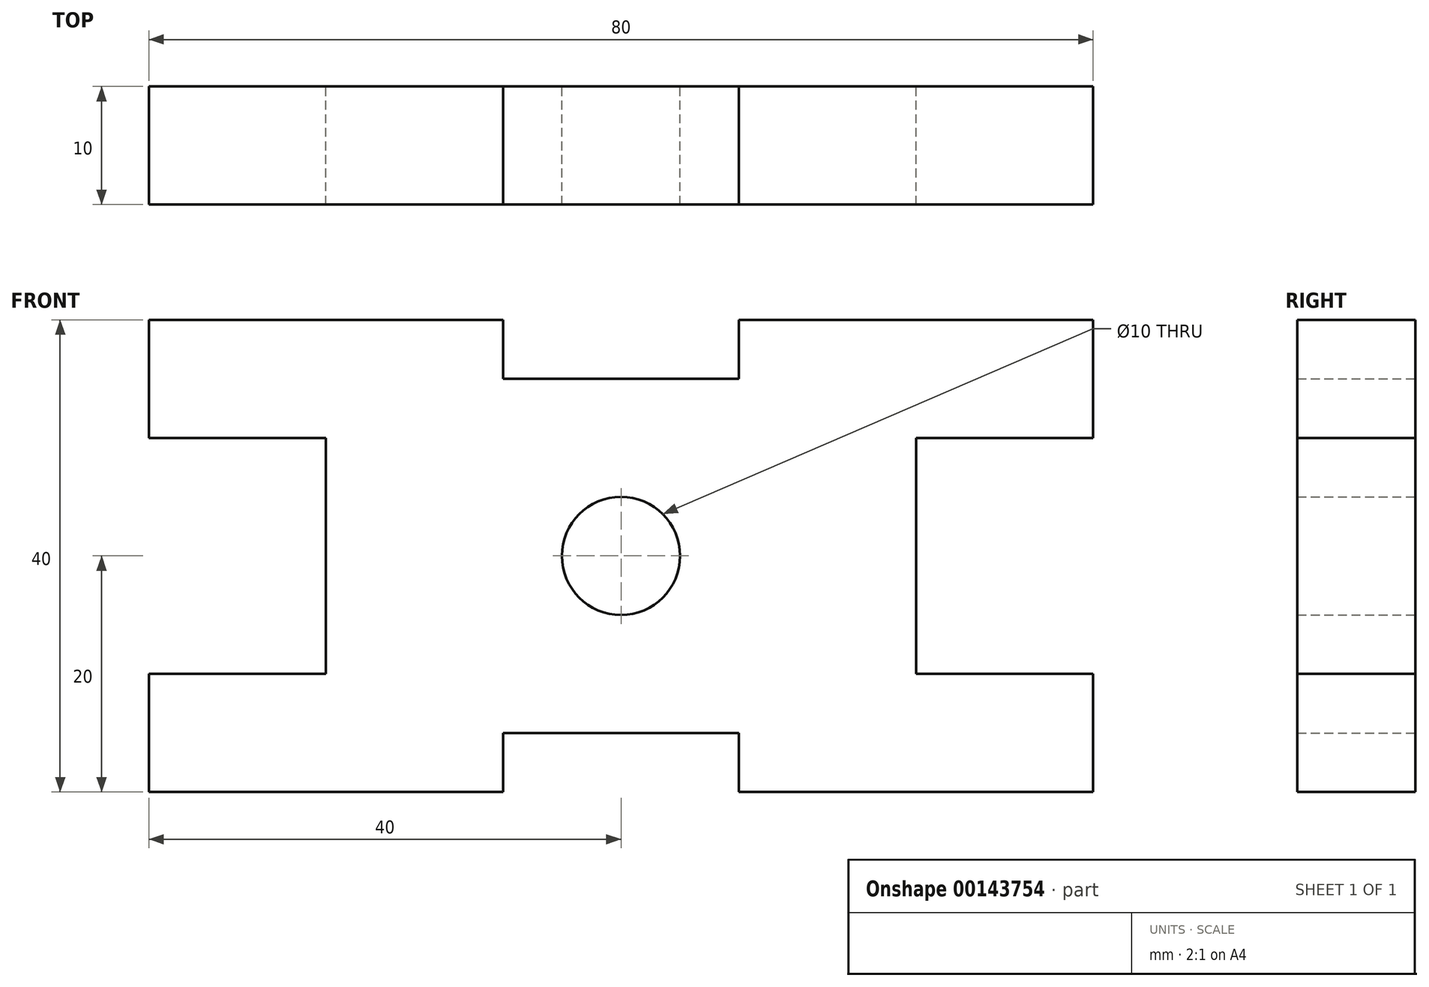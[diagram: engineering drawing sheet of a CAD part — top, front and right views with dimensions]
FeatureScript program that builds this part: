
annotation { "Feature Type Name" : "Feature", "Feature Type Description" : "" }
export const myFeature = defineFeature(function(context is Context, id is Id, definition is map)
    precondition{}
    {
        {
            var Q0;
            Q0=qCreatedBy(makeId("Front.planeOp"),FACE);
            var sketch = newSketch(context, id + "F0", { "sketchPlane" : qUnion([Q0])});
            skLineSegment(sketch, "E0", {"start": v(25, 10) * mm, "end": v(25, -10) * mm});
            skLineSegment(sketch, "E1", {"start": v(25, 10) * mm, "end": v(40, 10) * mm});
            skLineSegment(sketch, "E2", {"start": v(40, 10) * mm, "end": v(40, 20) * mm});
            skLineSegment(sketch, "E3", {"start": v(25, -10) * mm, "end": v(40, -10) * mm});
            skLineSegment(sketch, "E4", {"start": v(40, -10) * mm, "end": v(40, -20) * mm});
            skLineSegment(sketch, "E5", {"start": v(40, 20) * mm, "end": v(10, 20) * mm});
            skLineSegment(sketch, "E6", {"start": v(10, 20) * mm, "end": v(10, 15) * mm});
            skLineSegment(sketch, "E7", {"start": v(10, 15) * mm, "end": v(-10, 15) * mm});
            skLineSegment(sketch, "E8", {"start": v(-10, 15) * mm, "end": v(-10, 20) * mm});
            skLineSegment(sketch, "E9", {"start": v(-10, 20) * mm, "end": v(-40, 20) * mm});
            skLineSegment(sketch, "E10", {"start": v(-40, 20) * mm, "end": v(-40, 10) * mm});
            skLineSegment(sketch, "E11", {"start": v(-40, 10) * mm, "end": v(-25, 10) * mm});
            skLineSegment(sketch, "E12", {"start": v(-25, 10) * mm, "end": v(-25, -10) * mm});
            skLineSegment(sketch, "E13", {"start": v(-25, -10) * mm, "end": v(-40, -10) * mm});
            skLineSegment(sketch, "E14", {"start": v(-40, -10) * mm, "end": v(-40, -20) * mm});
            skLineSegment(sketch, "E15", {"start": v(-40, -20) * mm, "end": v(-10, -20) * mm});
            skLineSegment(sketch, "E16", {"start": v(-10, -20) * mm, "end": v(-10, -15) * mm});
            skLineSegment(sketch, "E17", {"start": v(-10, -15) * mm, "end": v(10, -15) * mm});
            skLineSegment(sketch, "E18", {"start": v(10, -15) * mm, "end": v(10, -20) * mm});
            skLineSegment(sketch, "E19", {"start": v(10, -20) * mm, "end": v(40, -20) * mm});
            skLineSegment(sketch, "E20", {"start": v(0, 15) * mm, "end": v(0, -15) * mm, "construction": true});
            skLineSegment(sketch, "E21", {"start": v(-25, 0) * mm, "end": v(25, 0) * mm, "construction": true});
            skCircle(sketch, "E22", {"center": v(0, 0) * mm, "radius": 5 * mm});
            skSolve(sketch);
        }
        {
            var Q0;
            Q0=qSketchRegion(id+"F0",true);
            extrude(context, id + "F1", {"entities" : qUnion([Q0]), "depth" : 10 * mm});
        }
    });
